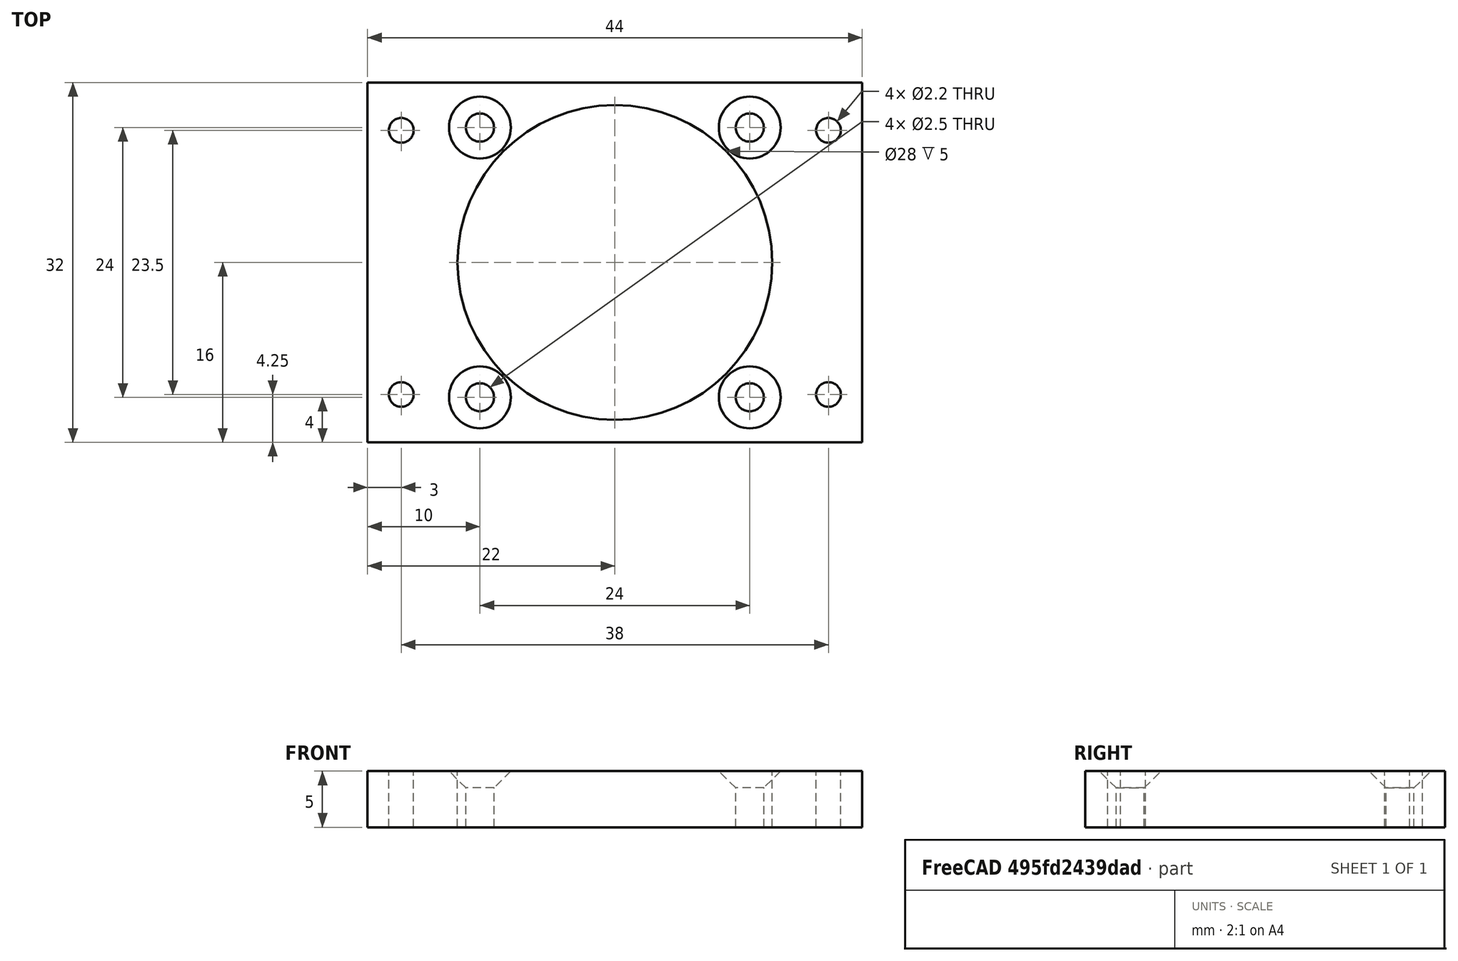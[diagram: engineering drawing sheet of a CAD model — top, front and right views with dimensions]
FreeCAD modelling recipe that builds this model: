
FCSTD DOCUMENT  (FreeCAD 0.16R)
Label: Camera Thing 0.1
License: All rights reserved
LicenseURL: http://en.wikipedia.org/wiki/All_rights_reserved
objects: Part::Cylinder×9, Part::Cut×3, Part::MultiFuse×2, Part::Chamfer×2, Part::Box×1
note: 17 computed .brp shape members not serialized (recipe doc carries the construction recipe); baked Part::Feature solids carry a one-line shape summary decoded from their .brp

FEATURE [Part::Box] Box  label="Cube"
  Height = 5
  Length = 44
  Placement = pos=(0,0,1) rot=(0,0,1;0rad)
  Width = 32
FEATURE [Part::Cylinder] Cylinder
  Angle = 360
  Height = 10
  Placement = pos=(22,16,-1) rot=(0,0,1;0rad)
  Radius = 14
FEATURE [Part::Cylinder] Cylinder001
  Angle = 360
  Height = 10
  Placement = pos=(10,4,0) rot=(0,0,1;0rad)
  Radius = 1.25
FEATURE [Part::Cylinder] Cylinder002
  Angle = 360
  Height = 10
  Placement = pos=(3,4.25,0) rot=(0,0,1;0rad)
  Radius = 1.1
FEATURE [Part::Cylinder] Cylinder003
  Angle = 360
  Height = 10
  Placement = pos=(3,27.75,0) rot=(0,0,1;0rad)
  Radius = 1.1
FEATURE [Part::Cylinder] Cylinder004
  Angle = 360
  Height = 10
  Placement = pos=(41,4.25,0) rot=(0,0,1;0rad)
  Radius = 1.1
FEATURE [Part::Cylinder] Cylinder005
  Angle = 360
  Height = 10
  Placement = pos=(41,27.75,0) rot=(0,0,1;0rad)
  Radius = 1.1
FEATURE [Part::Cylinder] Cylinder006
  Angle = 360
  Height = 10
  Placement = pos=(10,28,0) rot=(0,0,1;0rad)
  Radius = 1.25
FEATURE [Part::Cylinder] Cylinder007
  Angle = 360
  Height = 10
  Placement = pos=(34,28,0) rot=(0,0,1;0rad)
  Radius = 1.25
FEATURE [Part::Cylinder] Cylinder008
  Angle = 360
  Height = 10
  Placement = pos=(34,4,0) rot=(0,0,1;0rad)
  Radius = 1.25
FEATURE [Part::Cut] Cut
  Base = -> Box
  Tool = -> Cylinder
FEATURE [Part::MultiFuse] Fusion
  Shapes = -> [Cylinder002,Cylinder003,Cylinder004,Cylinder005]
FEATURE [Part::MultiFuse] Fusion001
  Shapes = -> [Cylinder001,Cylinder006,Cylinder007,Cylinder008]
FEATURE [Part::Cut] Cut001
  Base = -> Cut
  Tool = -> Fusion
FEATURE [Part::Cut] Cut002
  Base = -> Cut001
  Tool = -> Fusion001
FEATURE [Part::Chamfer] Chamfer
  Base = -> Cut002
  Edges = 1 edges r=1.5: [Edge16]
FEATURE [Part::Chamfer] Chamfer001
  Base = -> Chamfer
  Edges = 3 edges r=1.5: [Edge8,Edge10,Edge11]
